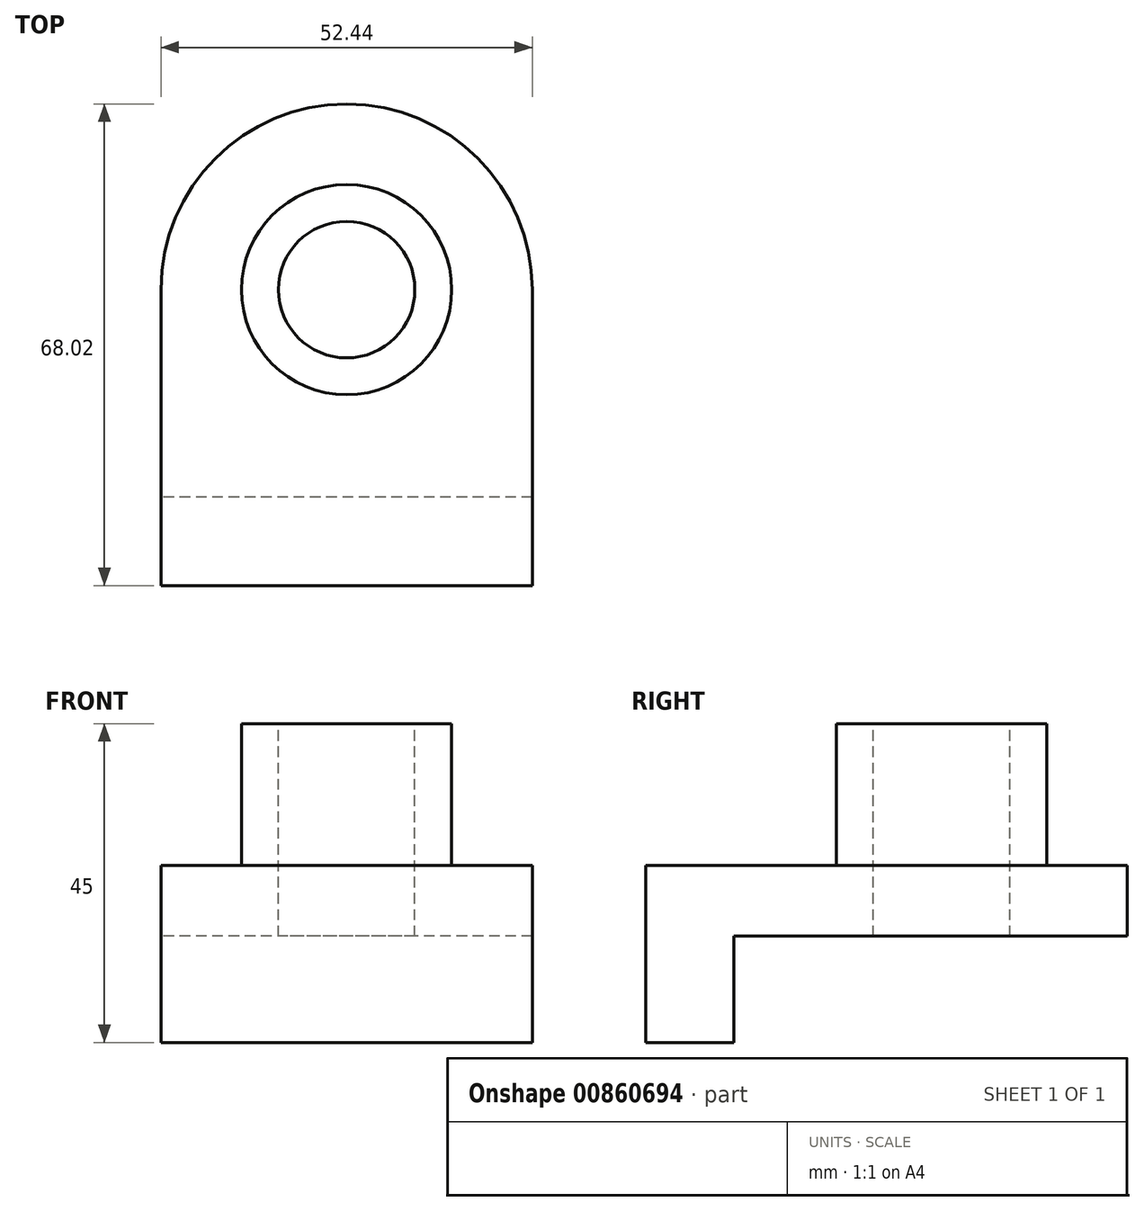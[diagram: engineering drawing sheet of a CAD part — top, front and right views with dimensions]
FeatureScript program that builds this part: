
annotation { "Feature Type Name" : "Feature", "Feature Type Description" : "" }
export const myFeature = defineFeature(function(context is Context, id is Id, definition is map)
    precondition{}
    {
        {
            var Q0;
            Q0=qCreatedBy(makeId("Top.planeOp"),FACE);
            var sketch = newSketch(context, id + "F0", { "sketchPlane" : qUnion([Q0])});
            skLineSegment(sketch, "E0.bottom", {"start": v(26.22, -6.25) * mm, "end": v(-26.22, -6.25) * mm});
            skLineSegment(sketch, "E0.top", {"start": v(26.22, 6.25) * mm, "end": v(-26.22, 6.25) * mm});
            skLineSegment(sketch, "E0.left", {"start": v(26.22, -6.25) * mm, "end": v(26.22, 6.25) * mm});
            skLineSegment(sketch, "E0.right", {"start": v(-26.22, -6.25) * mm, "end": v(-26.22, 6.25) * mm});
            skPoint(sketch, "E0.middle", {"position": v(0, 0) * mm});
            skSolve(sketch);
        }
        {
            var Q0;
            Q0=makeQuery(id+"F0.imprint","IMPRINT",FACE,{"disambiguationData":[TD([[makeQuery(id+"F0.imprint","IMPRINT",EDGE,{"derivedFrom":sQuery(id+"F0.wireOp",EDGE,"E0.bottom")}),-1.0]])]});
            extrude(context, id + "F1", {"entities" : qUnion([Q0]), "depth" : 15 * mm, "offsetDistance" : 25 * mm});
        }
        {
            var Q0;
            Q0=makeQuery(id+"F1.opExtrude","CAP_FACE",FACE,{"disambiguationData":[OSD([sQuery(id+"F0.wireOp",EDGE,"E0.bottom"),sQuery(id+"F0.wireOp",EDGE,"E0.top"),sQuery(id+"F0.wireOp",EDGE,"E0.left"),sQuery(id+"F0.wireOp",EDGE,"E0.right")])],"isStart":false});
            var sketch = newSketch(context, id + "F2", { "sketchPlane" : qUnion([Q0])});
            skLineSegment(sketch, "E1.bottom", {"start": v(-26.22, -6.25) * mm, "end": v(26.22, -6.25) * mm});
            skLineSegment(sketch, "E1.top", {"start": v(-26.22, 35.55) * mm, "end": v(26.22, 35.55) * mm});
            skLineSegment(sketch, "E1.left", {"start": v(-26.22, -6.25) * mm, "end": v(-26.22, 35.55) * mm});
            skLineSegment(sketch, "E1.right", {"start": v(26.22, -6.25) * mm, "end": v(26.22, 35.55) * mm});
            skSolve(sketch);
        }
        {
            var Q0;
            {var subQ0=sQuery(id+"F2.wireOp",EDGE,"E1.top");Q0=makeQuery(id+"F2.imprint","IMPRINT",FACE,{"disambiguationData":[TD([[makeQuery(id+"F2.imprint","IMPRINT",EDGE,{"derivedFrom":subQ0}),-1.0]])]});}
            var Q1;
            {var subQ0=sQuery(id+"F2.wireOp",EDGE,"E1.bottom");Q1=makeQuery(id+"F2.imprint","IMPRINT",FACE,{"disambiguationData":[TD([[makeQuery(id+"F2.imprint","IMPRINT",EDGE,{"derivedFrom":subQ0}),-1.0]])]});}
            extrude(context, id + "F3", {"entities" : qUnion([Q0, Q1]), "operationType" : NewBodyOperationType.ADD, "depth" : 10 * mm, "offsetDistance" : 25 * mm});
        }
        {
            var Q0;
            Q0=makeQuery(id+"F3.opExtrude","CAP_FACE",FACE,{"disambiguationData":[OSD([sQuery(id+"F2.wireOp",EDGE,"E1.bottom"),sQuery(id+"F2.wireOp",EDGE,"E1.top"),sQuery(id+"F2.wireOp",EDGE,"E1.left"),sQuery(id+"F2.wireOp",EDGE,"E1.right")])],"isStart":false});
            var sketch = newSketch(context, id + "F4", { "sketchPlane" : qUnion([Q0])});
            skArc(sketch, "E2", {"start": v(26.22, 35.55) * mm, "mid": v(0, 61.77) * mm, "end": v(-26.22, 35.55) * mm});
            skSolve(sketch);
        }
        {
            var Q0;
            Q0=makeQuery(id+"F4.imprint","IMPRINT",FACE,{"disambiguationData":[TD([[makeQuery(id+"F4.imprint","IMPRINT",EDGE,{"derivedFrom":sQuery(id+"F4.wireOp",EDGE,"E2")}),1.0]])]});
            extrude(context, id + "F5", {"entities" : qUnion([Q0]), "operationType" : NewBodyOperationType.ADD, "oppositeDirection" : true, "depth" : 10 * mm, "offsetDistance" : 25 * mm});
        }
        {
            var Q0;
            {var subQ0=sQuery(id+"F2.wireOp",EDGE,"E1.top");Q0=makeQuery(id+"F5.boolean.opBoolean","MERGE",FACE,{"derivedFrom":[makeQuery(id+"F3.opExtrude","CAP_FACE",FACE,{"disambiguationData":[OSD([sQuery(id+"F2.wireOp",EDGE,"E1.bottom"),subQ0,sQuery(id+"F2.wireOp",EDGE,"E1.left"),sQuery(id+"F2.wireOp",EDGE,"E1.right")])],"isStart":false}),makeQuery(id+"F5.opExtrude","CAP_FACE",FACE,{"disambiguationData":[OSD([subQ0,sQuery(id+"F4.wireOp",EDGE,"E2")])],"isStart":true})]});}
            var sketch = newSketch(context, id + "F6", { "sketchPlane" : qUnion([Q0])});
            skCircle(sketch, "E3", {"center": v(0, 35.55) * mm, "radius": 14.85 * mm});
            skSolve(sketch);
        }
        {
            var Q0;
            Q0=makeQuery(id+"F6.imprint","IMPRINT",FACE,{"disambiguationData":[TD([[makeQuery(id+"F6.imprint","IMPRINT",EDGE,{"derivedFrom":sQuery(id+"F6.wireOp",EDGE,"E3")}),1.0]])]});
            extrude(context, id + "F7", {"entities" : qUnion([Q0]), "operationType" : NewBodyOperationType.ADD, "depth" : 20 * mm, "offsetDistance" : 25 * mm});
        }
        {
            var Q0;
            Q0=makeQuery(id+"F7.opExtrude","CAP_FACE",FACE,{"disambiguationData":[OSD([sQuery(id+"F6.wireOp",EDGE,"E3")])],"isStart":false});
            var sketch = newSketch(context, id + "F8", { "sketchPlane" : qUnion([Q0])});
            skCircle(sketch, "E4", {"center": v(0, 35.55) * mm, "radius": 9.64 * mm});
            skSolve(sketch);
        }
        {
            var Q0;
            Q0=makeQuery(id+"F8.imprint","IMPRINT",FACE,{"disambiguationData":[TD([[makeQuery(id+"F8.imprint","IMPRINT",EDGE,{"derivedFrom":sQuery(id+"F8.wireOp",EDGE,"E4")}),1.0]])]});
            extrude(context, id + "F9", {"entities" : qUnion([Q0]), "operationType" : NewBodyOperationType.REMOVE, "endBound" : BoundingType.THROUGH_ALL, "oppositeDirection" : true, "depth" : 25 * mm, "offsetDistance" : 25 * mm});
        }
    });
